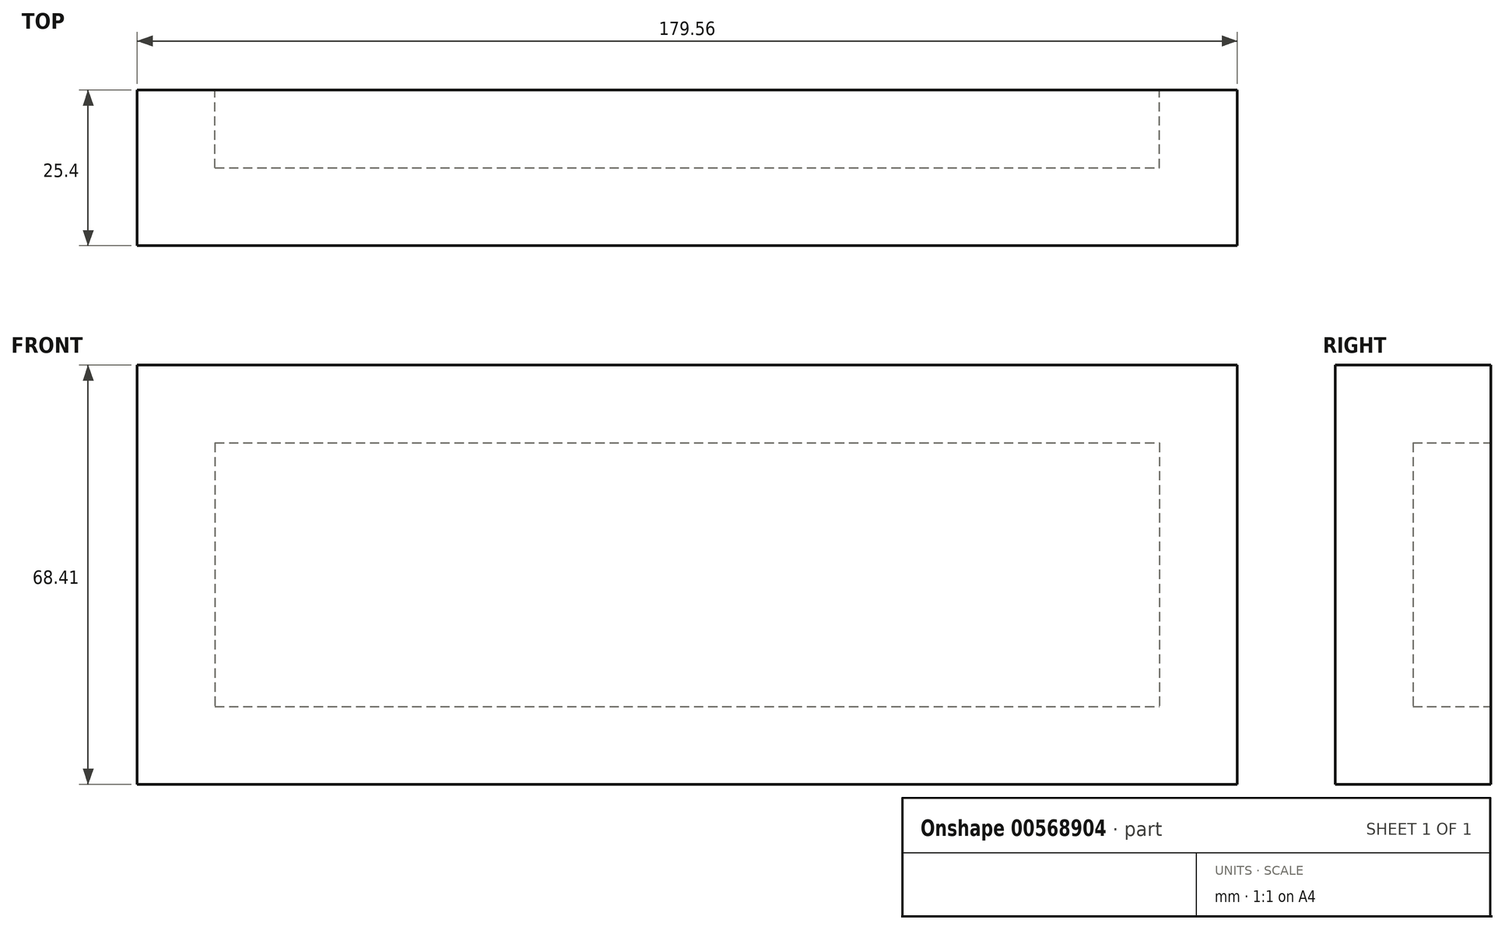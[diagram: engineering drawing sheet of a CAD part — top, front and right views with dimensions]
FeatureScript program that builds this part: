
annotation { "Feature Type Name" : "Feature", "Feature Type Description" : "" }
export const myFeature = defineFeature(function(context is Context, id is Id, definition is map)
    precondition{}
    {
        {
            var Q0;
            Q0=qCreatedBy(makeId("Front.planeOp"),FACE);
            var sketch = newSketch(context, id + "F0", { "sketchPlane" : qUnion([Q0])});
            skLineSegment(sketch, "E0.bottom", {"start": v(-87.64, 36.04) * mm, "end": v(91.92, 36.04) * mm});
            skLineSegment(sketch, "E0.top", {"start": v(-87.64, -32.37) * mm, "end": v(91.92, -32.37) * mm});
            skLineSegment(sketch, "E0.left", {"start": v(-87.64, 36.04) * mm, "end": v(-87.64, -32.37) * mm});
            skLineSegment(sketch, "E0.right", {"start": v(91.92, 36.04) * mm, "end": v(91.92, -32.37) * mm});
            skSolve(sketch);
        }
        {
            var Q0;
            Q0=makeQuery(id+"F0.imprint","IMPRINT",FACE,{"disambiguationData":[TD([[makeQuery(id+"F0.imprint","IMPRINT",EDGE,{"derivedFrom":sQuery(id+"F0.wireOp",EDGE,"E0.bottom")}),-1.0]])]});
            extrude(context, id + "F1", {"entities" : qUnion([Q0]), "depth" : 25.4 * mm, "offsetDistance" : 25.4 * mm});
        }
        {
            var Q0;
            Q0=makeQuery(id+"F1.opExtrude","CAP_FACE",FACE,{"disambiguationData":[OSD([sQuery(id+"F0.wireOp",EDGE,"E0.bottom"),sQuery(id+"F0.wireOp",EDGE,"E0.top"),sQuery(id+"F0.wireOp",EDGE,"E0.left"),sQuery(id+"F0.wireOp",EDGE,"E0.right")])],"isStart":true});
            shell(context, id + "F2", {"entities" : qUnion([Q0]), "thickness" : 12.7 * mm});
        }
    });
